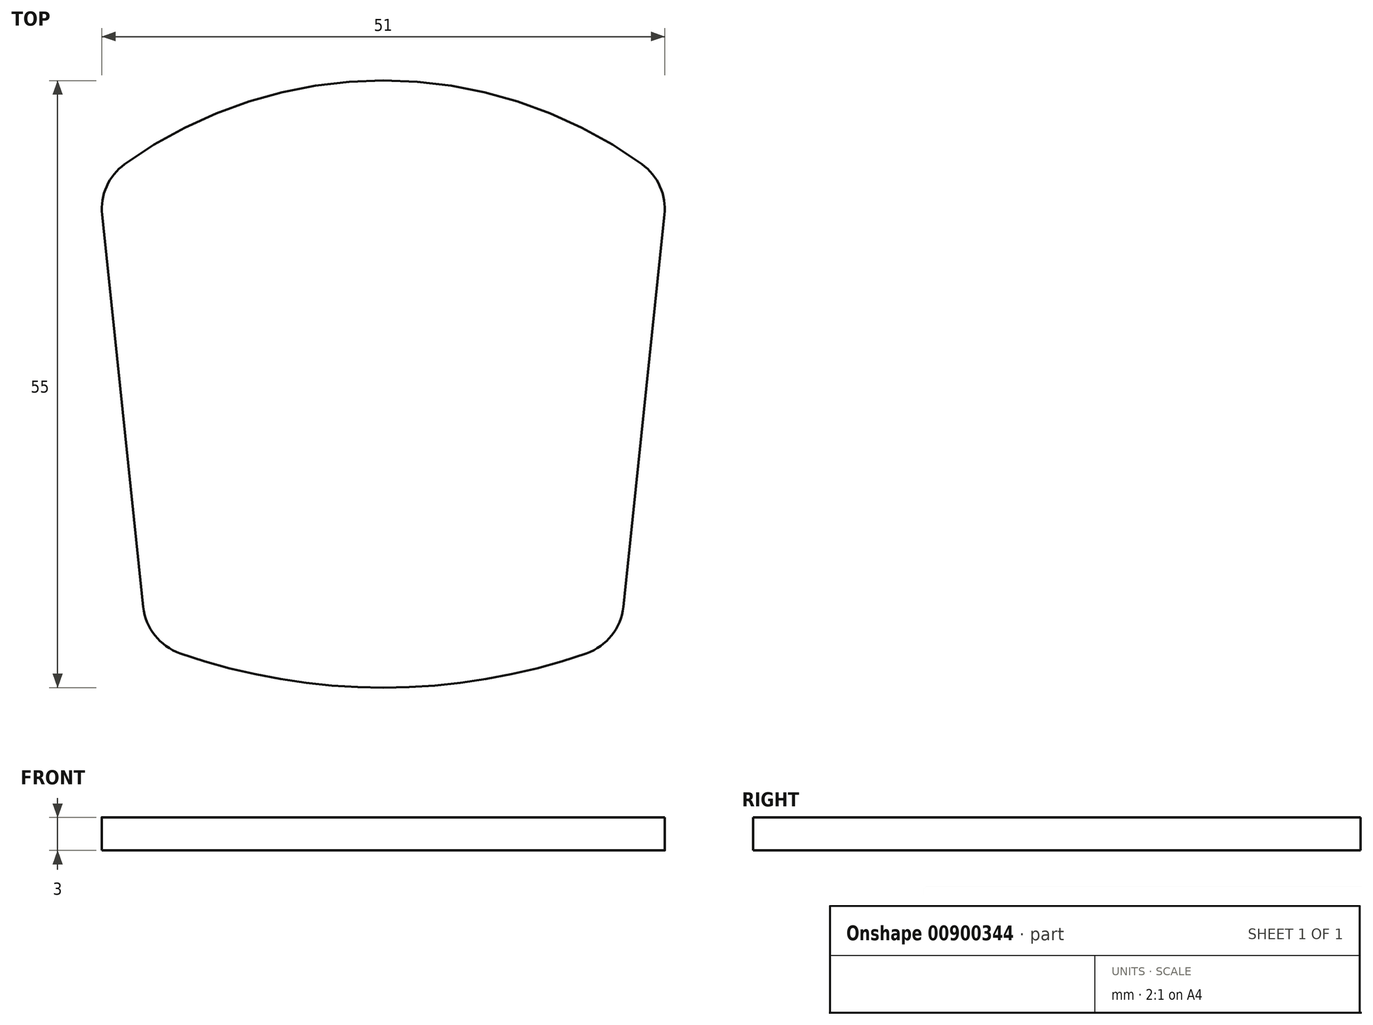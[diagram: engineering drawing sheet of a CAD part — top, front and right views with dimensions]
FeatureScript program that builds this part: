
annotation { "Feature Type Name" : "Feature", "Feature Type Description" : "" }
export const myFeature = defineFeature(function(context is Context, id is Id, definition is map)
    precondition{}
    {
        {
            var Q0;
            Q0=qCreatedBy(makeId("Top.planeOp"),FACE);
            var sketch = newSketch(context, id + "F0", { "sketchPlane" : qUnion([Q0])});
            skLineSegment(sketch, "E0", {"start": v(-21.74, 3.05) * mm, "end": v(-25.47, 38.59) * mm});
            skLineSegment(sketch, "E1", {"start": v(21.74, 3.05) * mm, "end": v(25.47, 38.59) * mm});
            skArc(sketch, "E2", {"start": v(23.43, 43.16) * mm, "mid": v(0, 50.74) * mm, "end": v(-23.43, 43.16) * mm});
            skArc(sketch, "E3", {"start": v(-18.4, -1.14) * mm, "mid": v(0, -4.26) * mm, "end": v(18.4, -1.14) * mm});
            skLineSegment(sketch, "E4.bottom", {"start": v(29.93, 52.93) * mm, "end": v(-29.93, 52.93) * mm, "construction": true});
            skLineSegment(sketch, "E4.top", {"start": v(29.93, -6.93) * mm, "end": v(-29.93, -6.93) * mm, "construction": true});
            skLineSegment(sketch, "E4.left", {"start": v(29.93, 52.93) * mm, "end": v(29.93, -6.93) * mm, "construction": true});
            skLineSegment(sketch, "E4.right", {"start": v(-29.93, 52.93) * mm, "end": v(-29.93, -6.93) * mm, "construction": true});
            skPoint(sketch, "E4.middle", {"position": v(0, 23) * mm});
            skPoint(sketch, "E5.visualSharp", {"position": v(-25.76, 41.34) * mm});
            skArc(sketch, "E5.filletArc", {"start": v(-23.43, 43.16) * mm, "mid": v(-25.07, 41.15) * mm, "end": v(-25.47, 38.59) * mm});
            skPoint(sketch, "E6.visualSharp", {"position": v(25.76, 41.34) * mm});
            skArc(sketch, "E6.filletArc", {"start": v(25.47, 38.59) * mm, "mid": v(25.07, 41.15) * mm, "end": v(23.43, 43.16) * mm});
            skPoint(sketch, "E7.visualSharp", {"position": v(21.42, 0) * mm});
            skArc(sketch, "E7.filletArc", {"start": v(18.4, -1.14) * mm, "mid": v(20.68, 0.47) * mm, "end": v(21.74, 3.05) * mm});
            skPoint(sketch, "E8.visualSharp", {"position": v(-21.42, 0) * mm});
            skArc(sketch, "E8.filletArc", {"start": v(-21.74, 3.05) * mm, "mid": v(-20.68, 0.47) * mm, "end": v(-18.4, -1.14) * mm});
            skCircle(sketch, "E9", {"center": v(-30, -22) * mm, "radius": 10 * mm, "construction": true});
            skCircle(sketch, "E10", {"center": v(-20.5, 39.11) * mm, "radius": 5 * mm, "construction": true});
            skCircle(sketch, "E11", {"center": v(20.5, 39.11) * mm, "radius": 5 * mm, "construction": true});
            skCircle(sketch, "E12", {"center": v(16.77, 3.58) * mm, "radius": 5 * mm, "construction": true});
            skCircle(sketch, "E13", {"center": v(-16.77, 3.58) * mm, "radius": 5 * mm, "construction": true});
            skCircle(sketch, "E14", {"center": v(-45, 48) * mm, "radius": 10 * mm, "construction": true});
            skSolve(sketch);
        }
        {
            var Q0;
            Q0=makeQuery(id+"F0.imprint","IMPRINT",FACE,{"disambiguationData":[TD([[makeQuery(id+"F0.imprint","IMPRINT",EDGE,{"derivedFrom":sQuery(id+"F0.wireOp",EDGE,"E0")}),-1.0]])]});
            extrude(context, id + "F1", {"entities" : qUnion([Q0]), "depth" : 3 * mm, "offsetDistance" : 25 * mm});
        }
    });
